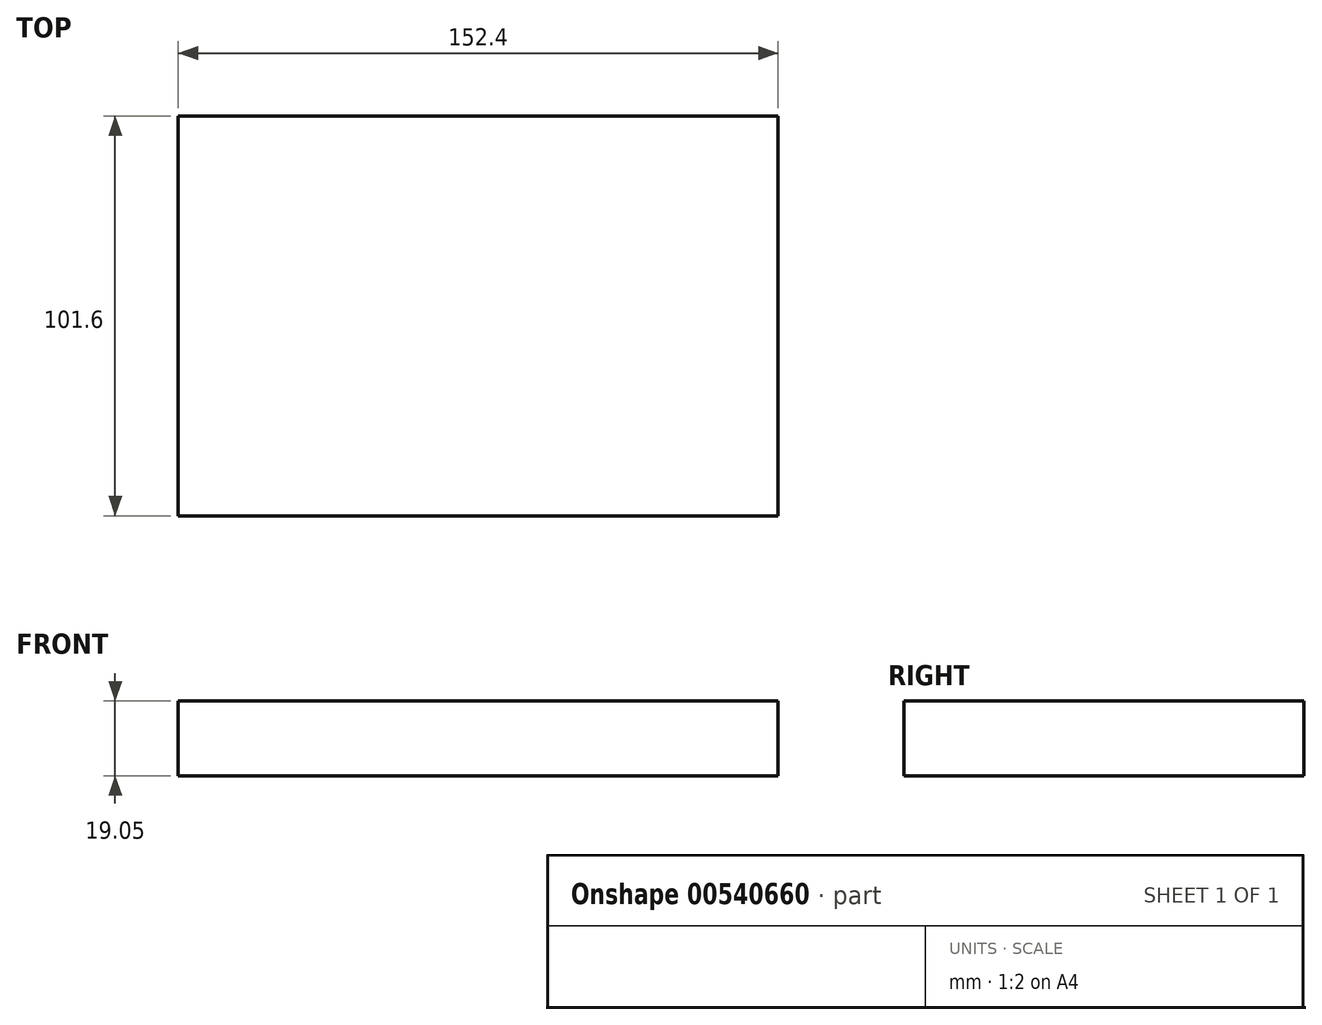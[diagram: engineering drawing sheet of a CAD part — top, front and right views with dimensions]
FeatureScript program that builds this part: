
annotation { "Feature Type Name" : "Feature", "Feature Type Description" : "" }
export const myFeature = defineFeature(function(context is Context, id is Id, definition is map)
    precondition{}
    {
        {
            var Q0;
            Q0=qCreatedBy(makeId("Top.planeOp"),FACE);
            var sketch = newSketch(context, id + "F0", { "sketchPlane" : qUnion([Q0])});
            skLineSegment(sketch, "E0.bottom", {"start": v(0, 0) * mm, "end": v(-152.4, 0) * mm});
            skLineSegment(sketch, "E0.top", {"start": v(0, 101.6) * mm, "end": v(-152.4, 101.6) * mm});
            skLineSegment(sketch, "E0.left", {"start": v(0, 0) * mm, "end": v(0, 101.6) * mm});
            skLineSegment(sketch, "E0.right", {"start": v(-152.4, 0) * mm, "end": v(-152.4, 101.6) * mm});
            skSolve(sketch);
        }
        {
            var Q0;
            Q0=makeQuery(id+"F0.imprint","IMPRINT",FACE,{"disambiguationData":[TD([[makeQuery(id+"F0.imprint","IMPRINT",EDGE,{"derivedFrom":sQuery(id+"F0.wireOp",EDGE,"E0.bottom")}),-1.0]])]});
            extrude(context, id + "F1", {"entities" : qUnion([Q0]), "depth" : 19.05 * mm, "offsetDistance" : 25.4 * mm});
        }
    });
